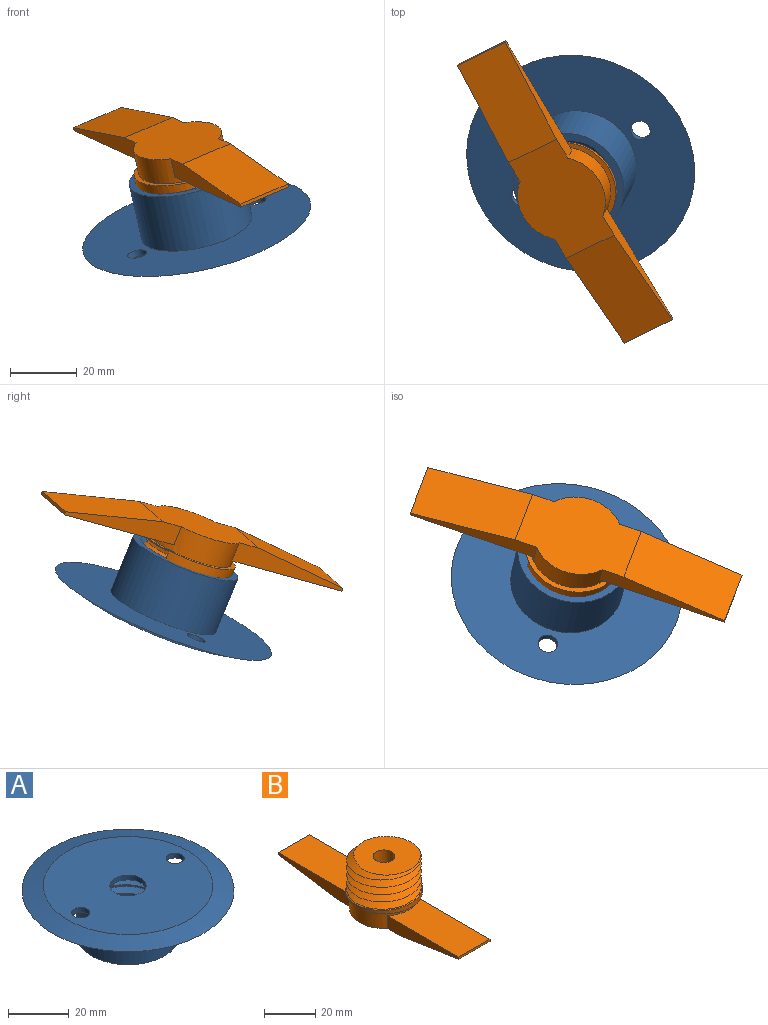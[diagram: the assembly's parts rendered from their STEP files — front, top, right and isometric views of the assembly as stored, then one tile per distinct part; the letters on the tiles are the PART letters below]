
ASSEMBLY  parts=2 mates=1
PART A: 13 faces, bbox 71.8x71.8x23.5 mm
  f0: cylinder r=12.3mm len=24.6mm, axis (0,0,1), area 353.7mm2, adj f1,f3,f4,f5,f8
  f1: plane 35.78x35.78mm, normal (0,0,-1), area 339.6mm2, adj f0,f2,f4,f5
  f2: cylinder r=16.99mm len=33.98mm, axis (0,0,1), area 1921.7mm2, adj f1,f6
  f3: plane 2.84x2.17mm, normal (0.78,-0.62,0), area 3.9mm2, adj f0,f4,f5
  f4: bspline ~34.76x30.1mm, area 1207mm2, adj f0,f1,f3,f5
  f5: bspline ~34.76x30.1mm, area 1314mm2, adj f0,f1,f3,f4,f8
  f6: plane 70x70mm, normal (0,0,-1), area 2884.9mm2, adj f2,f10,f11,f12
  f7: plane 56x56mm, normal (0,0,1), area 2293.4mm2, adj f9,f10,f11,f12
  f8: plane 24.6x24.6mm, normal (0,0,-1), area 362.3mm2, adj f0,f5,f9
  f9: cylinder r=6mm len=12mm, axis (0,0,1), area 75.4mm2, adj f7,f8
  f10: cone r=28mm half-angle=74.1deg, axis (0,0,-1), area 1440.9mm2, adj f6,f7
  f11: cylinder r=3mm len=6mm, axis (0,0,-1), area 37.7mm2, adj f6,f7
  f12: cylinder r=3mm len=6mm, axis (0,0,-1), area 37.7mm2, adj f6,f7
PART B: 24 faces, bbox 34.8x102.6x29.6 mm
  f0: plane 34.55x27mm, normal (0,0,-1), area 735.2mm2, adj f1,f4,f7,f8,f9,f22,f23
  f1: plane 39.57x6mm, normal (1,0,0), area 155.6mm2, adj f0,f2,f3,f9,f23
  f2: plane 39.57x17.14mm, normal (0,0,1), area 642.1mm2, adj f1,f3,f9,f22
  f3: plane 17.14x1mm, normal (0,-1,0), area 17.1mm2, adj f1,f2,f22,f23
  f4: plane 39.57x6mm, normal (1,0,0), area 155.6mm2, adj f0,f5,f6,f7,f9
  f5: plane 39.57x17.14mm, normal (0,0,1), area 642.1mm2, adj f4,f6,f8,f9
  f6: plane 17.14x1mm, normal (0,1,0), area 17.1mm2, adj f4,f5,f7,f8
  f7: plane 32.73x17.14mm, normal (0,0.15,-0.99), area 567.3mm2, adj f0,f4,f6,f8
  f8: plane 39.57x6mm, normal (-1,0,0), area 155.6mm2, adj f0,f5,f6,f7,f9
  f9: cylinder r=13.5mm len=27mm, axis (0,0,-1), area 455.8mm2, adj f0,f1,f2,f4,f5,f8,f10,f22
  f10: plane 30x30mm, normal (0,0,-1), area 134.3mm2, adj f9,f11
  f11: cylinder r=15mm len=30mm, axis (0,0,-1), area 164.9mm2, adj f10,f12,f21
  f12: bspline ~34.25x32.25mm, area 46.5mm2, adj f11,f13,f21
  f13: bspline ~29.12x29.11mm, area 1307.3mm2, adj f12,f14,f20,f21
  f14: plane 28.74x28.73mm, normal (0,0,1), area 480.8mm2, adj f13,f15,f20
  f15: cylinder r=4.25mm len=16.5mm, axis (0,0,1), area 434.9mm2, adj f14,f16,f17,f19
  f16: cylinder r=1.5mm len=3mm, axis (0,0.79,0.61), area 0mm2, adj f15,f17
  f17: cone r=1.5mm half-angle=3deg, axis (0,-0.79,-0.61), area 99.5mm2, adj f15,f16,f18
  f18: plane 3.95x3.13mm, normal (0,0.79,0.61), area 12.3mm2, adj f17
  f19: cone r=0mm half-angle=59deg, axis (0,0,1), area 66.2mm2, adj f15
  f20: bspline ~33.64x29.13mm, area 1155.5mm2, adj f13,f14,f21
  f21: plane 3.76x2.72mm, normal (-0.78,0.62,0), area 6.8mm2, adj f11,f12,f13,f20
  f22: plane 39.57x6mm, normal (-1,0,0), area 155.6mm2, adj f0,f2,f3,f9,f23
  f23: plane 32.73x17.14mm, normal (0,-0.15,-0.99), area 567.3mm2, adj f0,f1,f3,f22
PLACE A rot(axis=(-0.27,0.95,0.16),162.6deg) t=(-5.51,-10.11,24.69)mm
PLACE B rot(axis=(-0.24,0.96,0.16),163.1deg) t=(-6.26,-11.49,28.06)mm fixed
MATE cylindrical A.f2 <-> B.f9  axis (0.2,0.37,-0.91) through (-2.27,-4.17,10.19)mm
